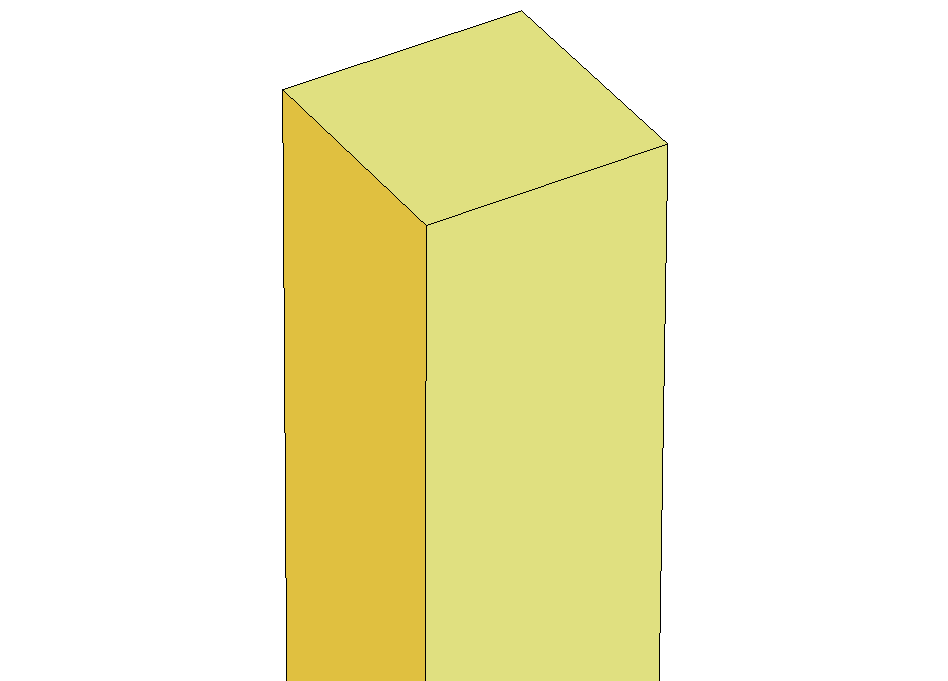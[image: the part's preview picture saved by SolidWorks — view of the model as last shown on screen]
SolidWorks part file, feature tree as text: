
SOLIDWORKS PART (.sldprt)
format: sldprt  version: not decoded by parser v0  size: 860,672 bytes
history: native  units: mm
features: sketch x8, fillet x5, cut_extrude x4, extrude x3, material x1, plane x1 (+13 scaffold rows collapsed)
feature tree (35):
  scaffold x13  (default folders/planes/origin — collapsed)
  material  "Material <not specified>"
  sketch  "Sketch stolphöjd"  dims[D1=1100.0mm D2=95.0mm]
  plane  "Lutande topplan"
  sketch  "Sketch2"  dims[D1=95.0mm]
  extrude  "Extrude höjd"  [1 undecoded]
  sketch  "Sketch10"  dims[D1=10.0mm D2=70.0mm]
  cut_extrude  "Cut-slits för stolpfot"  Depth=200mm
  sketch  "Sketch8"  dims[c1.D1=20.0mm c1.D2=20.0mm c1.D3=50.0mm c2.D1=177.5mm c2.D3=135.0mm c2.D4=1.0mm]
  cut_extrude  "Cut-skruvhål för stolpfot"  [1 undecoded]
  sketch  "Sketch12"
  extrude  "Extrude lutande topp"  [1 undecoded]
  sketch  "Sketch13"
  cut_extrude  "Cut-lutande topp"  [1 undecoded]
  sketch  "Sketch14"
  extrude  "Extrude tätraedertopp"  Depth=16mm
  sketch  "Sketch15"
  cut_extrude  "Cut-tapphål"  Depth=15mm
  fillet  "Fillet tätraeder"  Radius=3mm
  fillet  "Fillet lutande toppkanter"  Radius=3mm
  fillet  "Fille stolpkanter vid tetraeder"  Radius=3mm
  fillet  "Fillet stolpkanter vid lutande topp"  Radius=3mm
  fillet  "Fillet stolpkanter vid plan topp"  Radius=3mm
decode coverage: 12 of 20 modeling features carry decoded parameters
note: 4 parameter values undecoded
summary: no parameter record found for 4 features
note: suppression state not decoded; provenance and decode notes live in map.json
